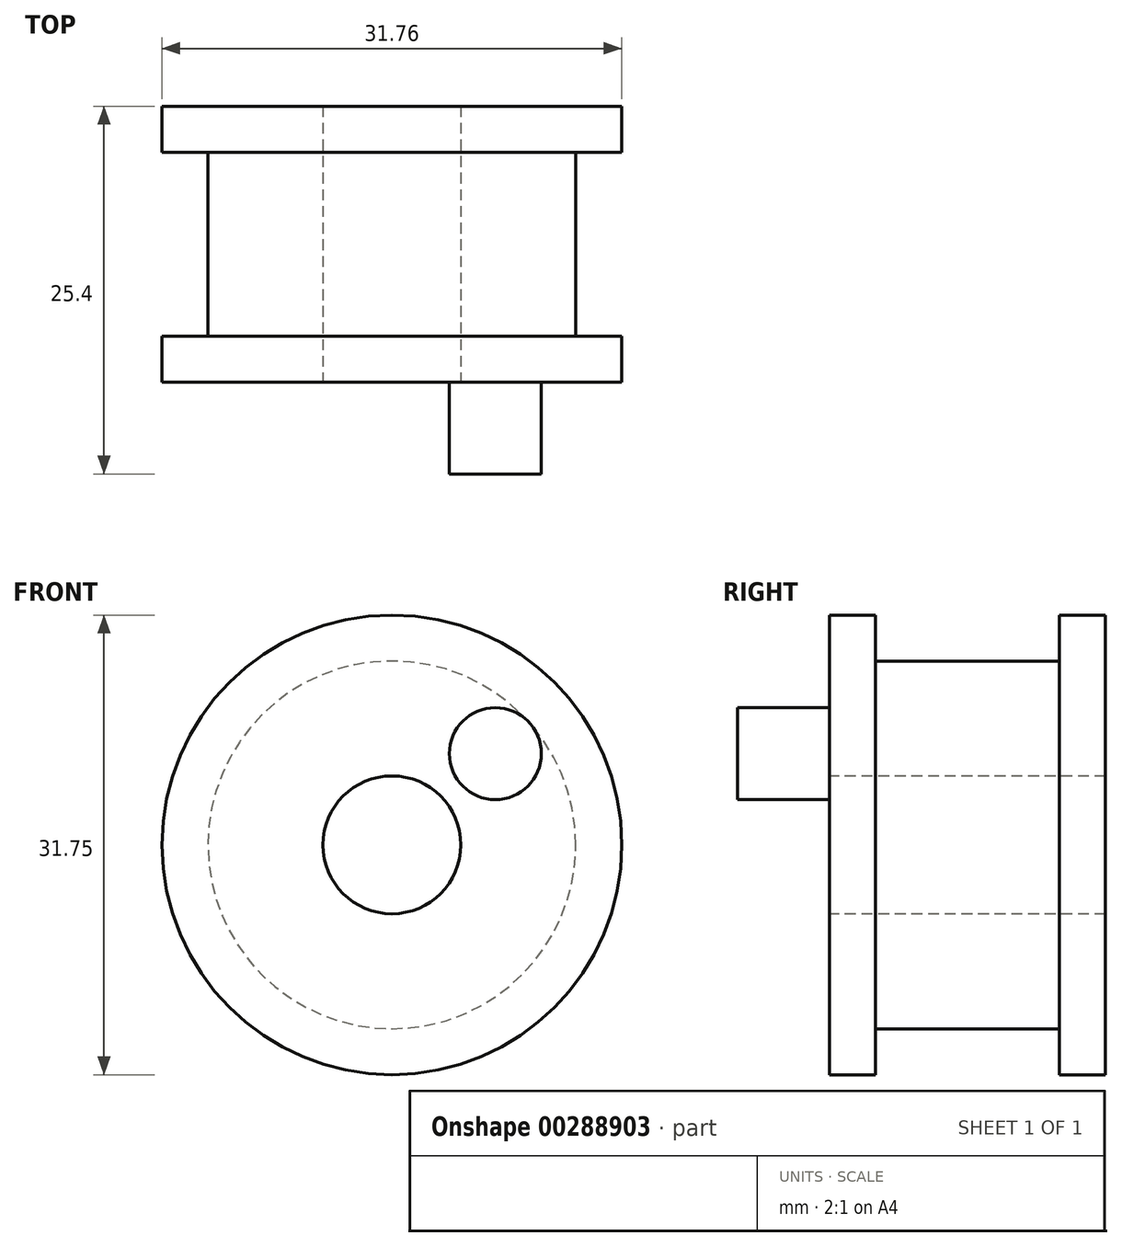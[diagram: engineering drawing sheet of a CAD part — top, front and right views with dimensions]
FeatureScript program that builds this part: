
annotation { "Feature Type Name" : "Feature", "Feature Type Description" : "" }
export const myFeature = defineFeature(function(context is Context, id is Id, definition is map)
    precondition{}
    {
        {
            var Q0;
            Q0=qCreatedBy(makeId("Right.planeOp"),FACE);
            var sketch = newSketch(context, id + "F0", { "sketchPlane" : qUnion([Q0])});
            skLineSegment(sketch, "E0.bottom", {"start": v(25.87, 12.36) * mm, "end": v(38.57, 12.36) * mm});
            skLineSegment(sketch, "E0.top", {"start": v(25.87, -0.34) * mm, "end": v(38.57, -0.34) * mm});
            skLineSegment(sketch, "E0.left", {"start": v(25.87, 12.36) * mm, "end": v(25.87, -0.34) * mm});
            skLineSegment(sketch, "E0.right", {"start": v(38.57, 12.36) * mm, "end": v(38.57, -0.34) * mm});
            skLineSegment(sketch, "E1.bottom", {"start": v(25.87, 12.36) * mm, "end": v(22.7, 12.36) * mm});
            skLineSegment(sketch, "E1.top", {"start": v(25.87, -3.52) * mm, "end": v(22.7, -3.52) * mm});
            skLineSegment(sketch, "E1.left", {"start": v(25.87, 12.36) * mm, "end": v(25.87, -3.52) * mm});
            skLineSegment(sketch, "E1.right", {"start": v(22.7, 12.36) * mm, "end": v(22.7, -3.52) * mm});
            skLineSegment(sketch, "E2.bottom", {"start": v(38.57, 12.36) * mm, "end": v(41.74, 12.36) * mm});
            skLineSegment(sketch, "E2.top", {"start": v(38.57, -3.52) * mm, "end": v(41.74, -3.52) * mm});
            skLineSegment(sketch, "E2.left", {"start": v(38.57, 12.36) * mm, "end": v(38.57, -3.52) * mm});
            skLineSegment(sketch, "E2.right", {"start": v(41.74, 12.36) * mm, "end": v(41.74, -3.52) * mm});
            skSolve(sketch);
        }
        {
            var Q0;
            {var subQ0=sQuery(id+"F0.wireOp",EDGE,"E0.bottom");Q0=makeQuery(id+"F0.imprint","IMPRINT",FACE,{"disambiguationData":[TD([[makeQuery(id+"F0.imprint","IMPRINT",EDGE,{"derivedFrom":subQ0}),-1.0]])]});}
            var Q1;
            {var subQ3=sQuery(id+"F0.wireOp",EDGE,"E2.bottom");Q1=makeQuery(id+"F0.imprint","IMPRINT",FACE,{"disambiguationData":[TD([[makeQuery(id+"F0.imprint","IMPRINT",EDGE,{"derivedFrom":subQ3}),-1.0]])]});}
            var Q2;
            {var subQ3=sQuery(id+"F0.wireOp",EDGE,"E1.bottom");Q2=makeQuery(id+"F0.imprint","IMPRINT",FACE,{"disambiguationData":[TD([[makeQuery(id+"F0.imprint","IMPRINT",EDGE,{"derivedFrom":subQ3}),1.0]])]});}
            var Q3;
            Q3=sQuery(id+"F0.wireOp",EDGE,"E0.bottom");
            revolve(context, id + "F1", {"entities" : qUnion([Q0, Q1, Q2]), "axis" : qUnion([Q3]), "revolveType" : RevolveType.FULL});
        }
        {
            var Q0;
            Q0=makeQuery(id+"F1.opRevolve","SWEPT_FACE",FACE,{"disambiguationData":[OSD([sQuery(id+"F0.wireOp",EDGE,"E1.right")])]});
            var sketch = newSketch(context, id + "F2", { "sketchPlane" : qUnion([Q0])});
            skCircle(sketch, "E3", {"center": v(0, 12.36) * mm, "radius": 4.76 * mm});
            skCircle(sketch, "E4", {"center": v(7.14, 18.66) * mm, "radius": 3.18 * mm});
            skSolve(sketch);
        }
        {
            var Q0;
            Q0=makeQuery(id+"F2.imprint","IMPRINT",FACE,{"disambiguationData":[TD([[makeQuery(id+"F2.imprint","IMPRINT",EDGE,{"derivedFrom":sQuery(id+"F2.wireOp",EDGE,"E4")}),1.0]])]});
            extrude(context, id + "F3", {"entities" : qUnion([Q0]), "operationType" : NewBodyOperationType.ADD, "depth" : 6.35 * mm});
        }
        {
            var Q0;
            Q0=sQuery(id+"F2.wireOp",VERTEX,"E3.center");
            var Q1;
            Q1=makeQuery(id+"F1.opRevolve","SWEPT_BODY",BODY,{"disambiguationData":[OSD([sQuery(id+"F0.wireOp",EDGE,"E0.bottom"),sQuery(id+"F0.wireOp",EDGE,"E0.top"),sQuery(id+"F0.wireOp",EDGE,"E1.bottom"),sQuery(id+"F0.wireOp",EDGE,"E1.top"),sQuery(id+"F0.wireOp",EDGE,"E1.left"),sQuery(id+"F0.wireOp",EDGE,"E1.right"),sQuery(id+"F0.wireOp",EDGE,"E2.bottom"),sQuery(id+"F0.wireOp",EDGE,"E2.top"),sQuery(id+"F0.wireOp",EDGE,"E2.left"),sQuery(id+"F0.wireOp",EDGE,"E2.right")])]});
            hole(context, id + "F4", {"style" : HoleStyle.SIMPLE, "endStyle" : HoleEndStyle.THROUGH, "holeDiameter" : 9.52 * mm, "tappedDepth" : 12.7 * mm, "tapClearance" : 3, "locations" : qUnion([Q0]), "scope" : qUnion([Q1])});
        }
    });
